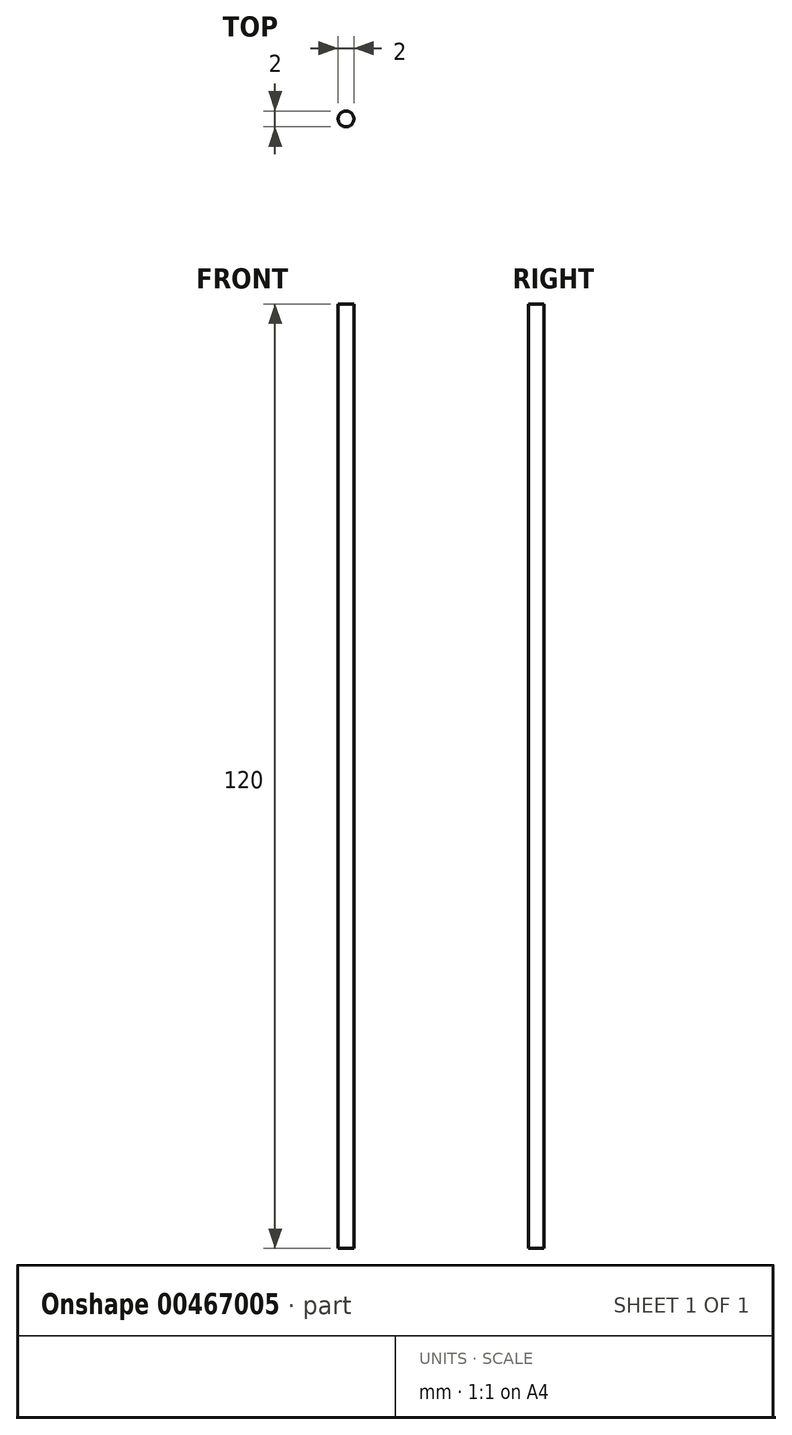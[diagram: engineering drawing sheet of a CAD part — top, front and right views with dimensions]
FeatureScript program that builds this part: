
annotation { "Feature Type Name" : "Feature", "Feature Type Description" : "" }
export const myFeature = defineFeature(function(context is Context, id is Id, definition is map)
    precondition{}
    {
        {
            var Q0;
            Q0=qCreatedBy(makeId("Top.planeOp"),FACE);
            var sketch = newSketch(context, id + "F0", { "sketchPlane" : qUnion([Q0])});
            skCircle(sketch, "E0", {"center": v(0, 0) * mm, "radius": 1 * mm});
            skSolve(sketch);
        }
        {
            var Q0;
            Q0=makeQuery(id+"F0.imprint","IMPRINT",FACE,{"disambiguationData":[TD([[makeQuery(id+"F0.imprint","IMPRINT",EDGE,{"derivedFrom":sQuery(id+"F0.wireOp",EDGE,"E0")}),1.0]])]});
            extrude(context, id + "F1", {"entities" : qUnion([Q0]), "depth" : 120 * mm});
        }
    });
